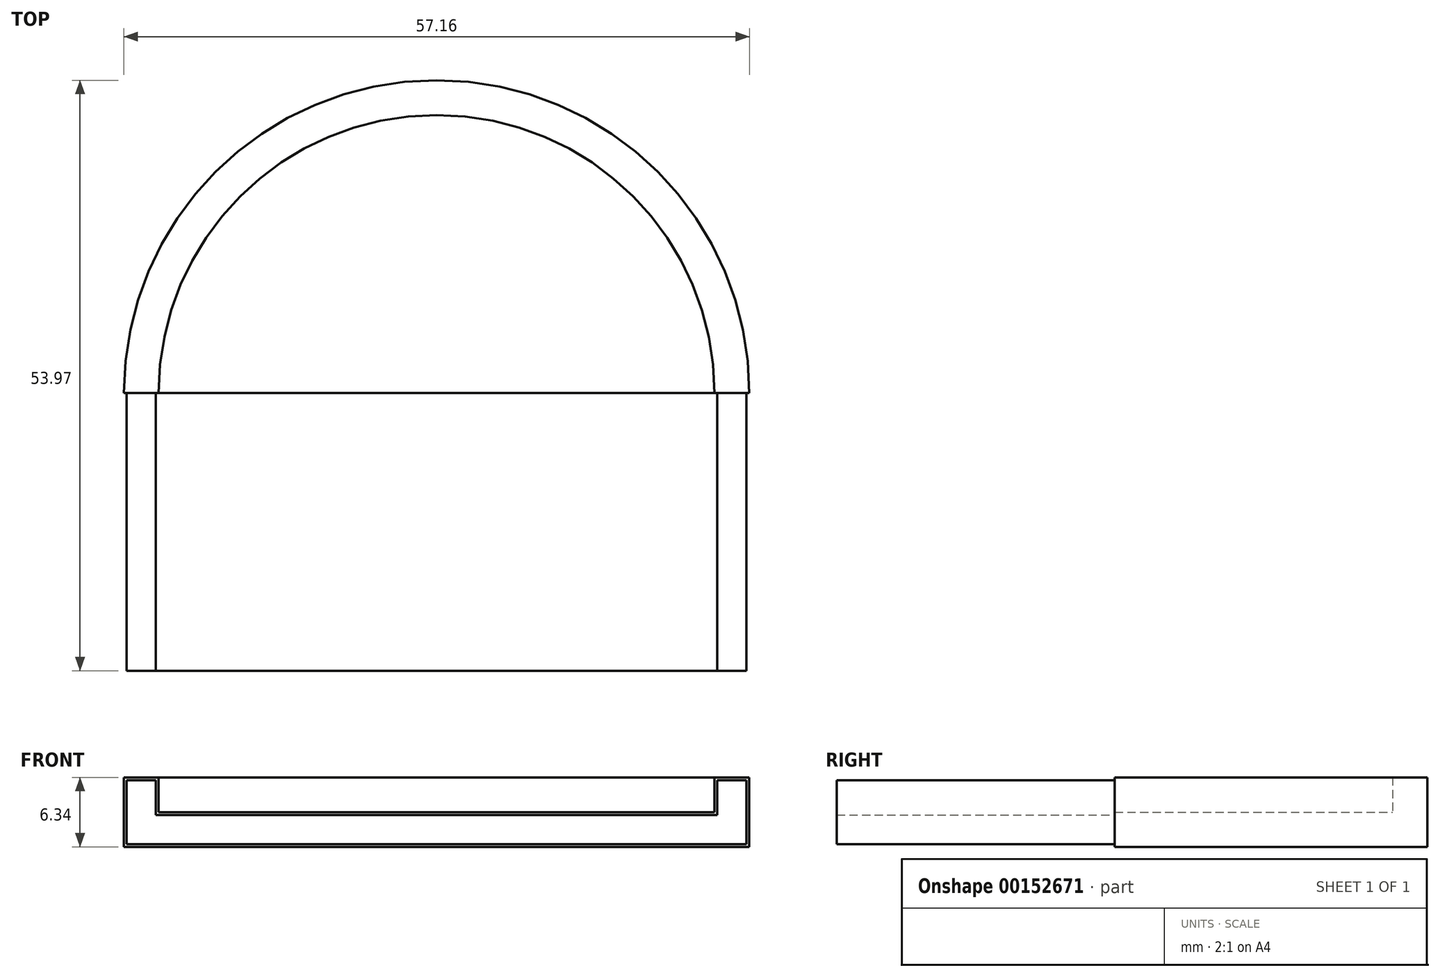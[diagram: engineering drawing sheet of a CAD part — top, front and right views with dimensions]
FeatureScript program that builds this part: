
annotation { "Feature Type Name" : "Feature", "Feature Type Description" : "" }
export const myFeature = defineFeature(function(context is Context, id is Id, definition is map)
    precondition{}
    {
        {
            var Q0;
            Q0=qCreatedBy(makeId("Top.planeOp"),FACE);
            var sketch = newSketch(context, id + "F0", { "sketchPlane" : qUnion([Q0])});
            skLineSegment(sketch, "E0.bottom", {"start": v(0, 0) * mm, "end": v(-3.18, 0) * mm});
            skLineSegment(sketch, "E0.top", {"start": v(0, 25.4) * mm, "end": v(-3.18, 25.4) * mm, "construction": true});
            skLineSegment(sketch, "E0.left", {"start": v(0, 0) * mm, "end": v(0, 25.4) * mm});
            skLineSegment(sketch, "E0.right", {"start": v(-3.17, 0) * mm, "end": v(-3.18, 25.4) * mm});
            skLineSegment(sketch, "E1", {"start": v(0, 25.4) * mm, "end": v(50.8, 25.4) * mm, "construction": true});
            skLineSegment(sketch, "E2.bottom", {"start": v(50.8, 25.4) * mm, "end": v(53.97, 25.4) * mm, "construction": true});
            skLineSegment(sketch, "E2.top", {"start": v(50.8, 0) * mm, "end": v(53.98, 0) * mm});
            skLineSegment(sketch, "E2.left", {"start": v(50.8, 25.4) * mm, "end": v(50.8, 0) * mm});
            skLineSegment(sketch, "E2.right", {"start": v(53.98, 25.4) * mm, "end": v(53.98, 0) * mm});
            skArc(sketch, "E3", {"start": v(50.8, 25.4) * mm, "mid": v(25.4, 50.8) * mm, "end": v(0, 25.4) * mm});
            skArc(sketch, "E4", {"start": v(53.98, 25.4) * mm, "mid": v(25.4, 53.98) * mm, "end": v(-3.18, 25.4) * mm});
            skSolve(sketch);
        }
        {
            var Q0;
            Q0=qSketchRegion(id+"F0",true);
            extrude(context, id + "F1", {"entities" : qUnion([Q0]), "depth" : 3.17 * mm});
        }
        {
            var Q0;
            Q0=makeQuery(id+"F1.opExtrude","CAP_FACE",FACE,{"disambiguationData":[OSD([sQuery(id+"F0.wireOp",EDGE,"E0.bottom"),sQuery(id+"F0.wireOp",EDGE,"E0.left"),sQuery(id+"F0.wireOp",EDGE,"E0.right"),sQuery(id+"F0.wireOp",EDGE,"E2.top"),sQuery(id+"F0.wireOp",EDGE,"E2.left"),sQuery(id+"F0.wireOp",EDGE,"E2.right"),sQuery(id+"F0.wireOp",EDGE,"E3"),sQuery(id+"F0.wireOp",EDGE,"E4")])],"isStart":true});
            var sketch = newSketch(context, id + "F2", { "sketchPlane" : qUnion([Q0])});
            skLineSegment(sketch, "E5.bottom", {"start": v(53.98, 0) * mm, "end": v(-3.18, 0) * mm});
            skLineSegment(sketch, "E5.top", {"start": v(53.98, -25.4) * mm, "end": v(-3.18, -25.4) * mm, "construction": true});
            skLineSegment(sketch, "E5.left", {"start": v(53.98, 0) * mm, "end": v(53.98, -25.4) * mm});
            skLineSegment(sketch, "E5.right", {"start": v(-3.18, 0) * mm, "end": v(-3.18, -25.4) * mm});
            skArc(sketch, "E6", {"start": v(-3.18, -25.4) * mm, "mid": v(25.4, -53.98) * mm, "end": v(53.98, -25.4) * mm});
            skSolve(sketch);
        }
        {
            var Q0;
            Q0=qSketchRegion(id+"F2",true);
            extrude(context, id + "F3", {"entities" : qUnion([Q0]), "operationType" : NewBodyOperationType.ADD, "depth" : 3.17 * mm});
        }
        {
            var Q0;
            Q0=makeQuery(id+"F1.opExtrude","CAP_FACE",FACE,{"disambiguationData":[OSD([sQuery(id+"F0.wireOp",EDGE,"E0.bottom"),sQuery(id+"F0.wireOp",EDGE,"E0.left"),sQuery(id+"F0.wireOp",EDGE,"E0.right"),sQuery(id+"F0.wireOp",EDGE,"E2.top"),sQuery(id+"F0.wireOp",EDGE,"E2.left"),sQuery(id+"F0.wireOp",EDGE,"E2.right"),sQuery(id+"F0.wireOp",EDGE,"E3"),sQuery(id+"F0.wireOp",EDGE,"E4")])],"isStart":false});
            var sketch = newSketch(context, id + "F4", { "sketchPlane" : qUnion([Q0])});
            skLineSegment(sketch, "E7.bottom", {"start": v(-3.17, 0) * mm, "end": v(-2.92, 0) * mm});
            skLineSegment(sketch, "E7.top", {"start": v(-3.18, 25.4) * mm, "end": v(-2.92, 25.4) * mm});
            skLineSegment(sketch, "E7.left", {"start": v(-3.17, 0) * mm, "end": v(-3.17, 25.4) * mm});
            skLineSegment(sketch, "E7.right", {"start": v(-2.92, 0) * mm, "end": v(-2.92, 25.4) * mm});
            skSolve(sketch);
        }
        {
            var Q0;
            Q0=makeQuery(id+"F4.imprint","IMPRINT",FACE,{"disambiguationData":[TD([[makeQuery(id+"F4.imprint","IMPRINT",EDGE,{"derivedFrom":sQuery(id+"F4.wireOp",EDGE,"E7.bottom")}),-1.0]])]});
            var Q1;
            Q1=makeQuery(id+"F3.boolean.opBoolean","MERGE",EDGE,{"derivedFrom":[makeQuery(id+"F1.opExtrude","SWEPT_EDGE",EDGE,{"disambiguationData":[OSD([sQuery(id+"F0.wireOp",EDGE,"E0.bottom"),sQuery(id+"F0.wireOp",EDGE,"E0.right")])]}),makeQuery(id+"F3.opExtrude","SWEPT_EDGE",EDGE,{"disambiguationData":[OSD([sQuery(id+"F2.wireOp",EDGE,"E5.bottom"),sQuery(id+"F2.wireOp",EDGE,"E5.right")])]})]});
            var Q2;
            Q2=makeQuery(id+"F3.opExtrude","CAP_EDGE",EDGE,{"disambiguationData":[OSD([sQuery(id+"F2.wireOp",EDGE,"E5.bottom")])],"isStart":false});
            var Q3;
            Q3=makeQuery(id+"F3.boolean.opBoolean","MERGE",EDGE,{"derivedFrom":[makeQuery(id+"F1.opExtrude","SWEPT_EDGE",EDGE,{"disambiguationData":[OSD([sQuery(id+"F0.wireOp",EDGE,"E2.top"),sQuery(id+"F0.wireOp",EDGE,"E2.right")])]}),makeQuery(id+"F3.opExtrude","SWEPT_EDGE",EDGE,{"disambiguationData":[OSD([sQuery(id+"F2.wireOp",EDGE,"E5.bottom"),sQuery(id+"F2.wireOp",EDGE,"E5.left")])]})]});
            var Q4;
            Q4=makeQuery(id+"F1.opExtrude","CAP_EDGE",EDGE,{"disambiguationData":[OSD([sQuery(id+"F0.wireOp",EDGE,"E2.top")])],"isStart":false});
            var Q5;
            Q5=makeQuery(id+"F1.opExtrude","SWEPT_EDGE",EDGE,{"disambiguationData":[OSD([sQuery(id+"F0.wireOp",EDGE,"E2.top"),sQuery(id+"F0.wireOp",EDGE,"E2.left")])]});
            var Q6;
            Q6=makeQuery(id+"F3.opExtrude","CAP_EDGE",EDGE,{"disambiguationData":[OSD([sQuery(id+"F2.wireOp",EDGE,"E5.bottom")])],"isStart":true});
            var Q7;
            Q7=makeQuery(id+"F1.opExtrude","SWEPT_EDGE",EDGE,{"disambiguationData":[OSD([sQuery(id+"F0.wireOp",EDGE,"E0.bottom"),sQuery(id+"F0.wireOp",EDGE,"E0.left")])]});
            var Q8;
            Q8=makeQuery(id+"F1.opExtrude","CAP_EDGE",EDGE,{"disambiguationData":[OSD([sQuery(id+"F0.wireOp",EDGE,"E0.bottom")])],"isStart":false});
            sweep(context, id + "F5", {"operationType" : NewBodyOperationType.REMOVE, "profiles" : qUnion([Q0]), "path" : qUnion([Q1, Q2, Q3, Q4, Q5, Q6, Q7, Q8])});
        }
    });
